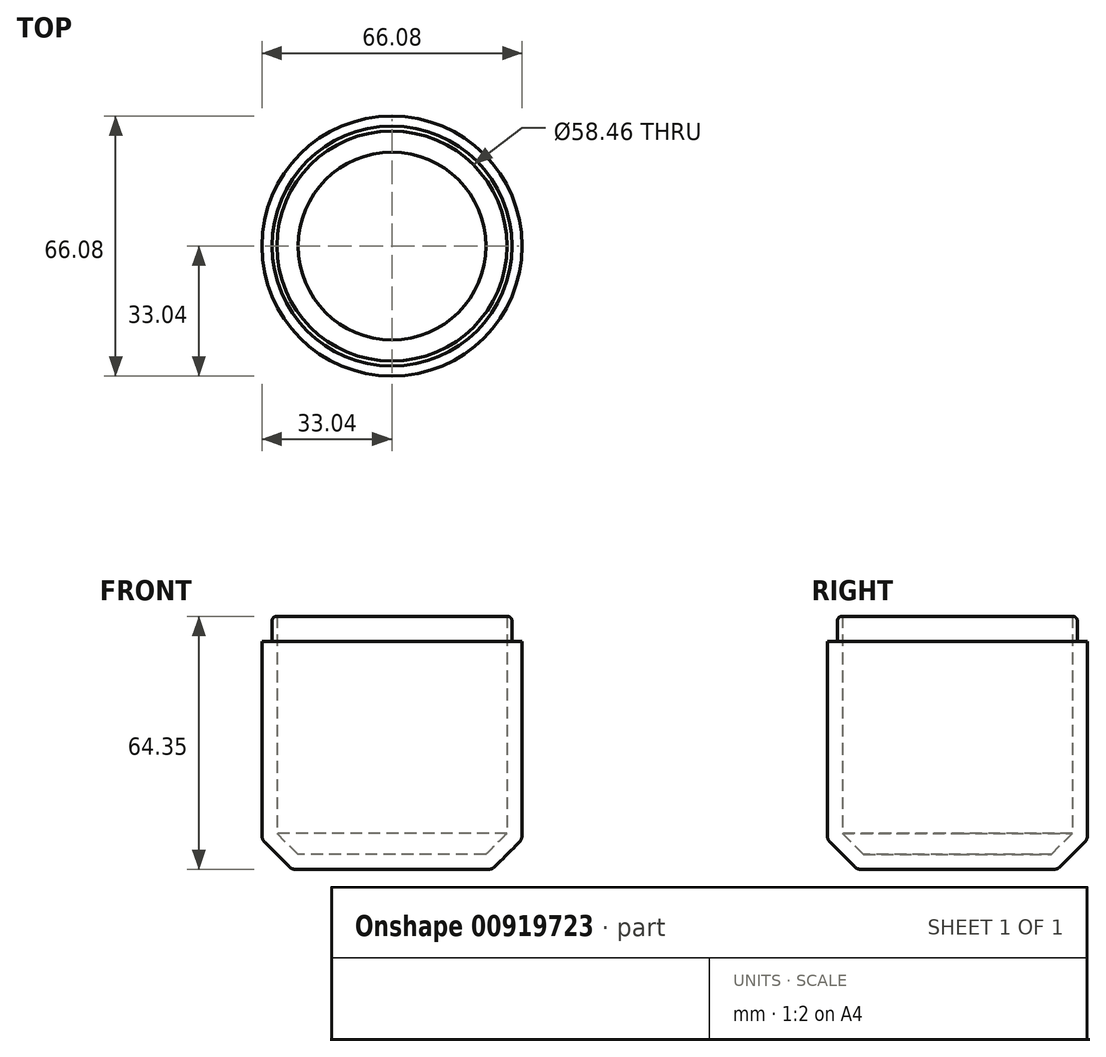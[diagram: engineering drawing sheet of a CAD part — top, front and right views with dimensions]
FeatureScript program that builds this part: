
annotation { "Feature Type Name" : "Feature", "Feature Type Description" : "" }
export const myFeature = defineFeature(function(context is Context, id is Id, definition is map)
    precondition{}
    {
        {
            var Q0;
            Q0=qCreatedBy(makeId("Top.planeOp"),FACE);
            var sketch = newSketch(context, id + "F0", { "sketchPlane" : qUnion([Q0])});
            skCircle(sketch, "E0", {"center": v(0, 0) * mm, "radius": 33.04 * mm});
            skSolve(sketch);
        }
        {
            var Q0;
            Q0 = qSketchRegion(id + "F0", true);
            extrude(context, id + "F1", {"entities" : qUnion([Q0]), "depth" : 58 * mm, "offsetDistance" : 25.4 * mm});
        }
        {
            var Q0;
            Q0=makeQuery(id+"F1.opExtrude","CAP_EDGE",EDGE,{"disambiguationData":[OSD([sQuery(id+"F0.wireOp",EDGE,"E0")])],"isStart":true});
            chamfer(context, id + "F2", {"entities" : qUnion([Q0]), "width" : 7.62 * mm, "tangentPropagation" : true});
        }
        {
            var Q0;
            Q0=makeQuery(id+"F1.opExtrude","CAP_FACE",FACE,{"disambiguationData":[OSD([sQuery(id+"F0.wireOp",EDGE,"E0")])],"isStart":false});
            shell(context, id + "F3", {"entities" : qUnion([Q0]), "thickness" : 3.8 * mm});
        }
        {
            var Q0;
            {var subQ0=sQuery(id+"F0.wireOp",EDGE,"E0");Q0=makeQuery(id+"F2.opChamfer","BLEND_EDGE",EDGE,{"blendedFrom":[makeQuery(id+"F1.opExtrude","CAP_EDGE",EDGE,{"disambiguationData":[OSD([subQ0])],"isStart":true}),makeQuery(id+"F1.opExtrude","SWEPT_FACE",FACE,{"disambiguationData":[OSD([subQ0])]})],"blendedInto":[makeQuery(id+"F1.opExtrude","SWEPT_FACE",FACE,{"disambiguationData":[OSD([subQ0])]})]});}
            var Q1;
            {var subQ0=sQuery(id+"F0.wireOp",EDGE,"E0");Q1=makeQuery(id+"F2.opChamfer","BLEND_EDGE",EDGE,{"blendedFrom":[makeQuery(id+"F1.opExtrude","CAP_EDGE",EDGE,{"disambiguationData":[OSD([subQ0])],"isStart":true}),makeQuery(id+"F1.opExtrude","CAP_FACE",FACE,{"disambiguationData":[OSD([subQ0])],"isStart":true})],"blendedInto":[makeQuery(id+"F1.opExtrude","CAP_FACE",FACE,{"disambiguationData":[OSD([subQ0])],"isStart":true})]});}
            fillet(context, id + "F4", {"entities" : qUnion([Q0, Q1]), "radius" : 2.54 * mm, "tangentPropagation" : true, "allowEdgeOverflow" : false});
        }
        {
            var Q0;
            Q0=makeQuery(id+"F1.opExtrude","CAP_FACE",FACE,{"disambiguationData":[OSD([sQuery(id+"F0.wireOp",EDGE,"E0")])],"isStart":false});
            var sketch = newSketch(context, id + "F5", { "sketchPlane" : qUnion([Q0])});
            skCircle(sketch, "E1", {"center": v(0, 0) * mm, "radius": 30.5 * mm});
            skCircle(sketch, "E2.0", {"center": v(0, 0) * mm, "radius": 29.23 * mm});
            skSolve(sketch);
        }
        {
            var Q0;
            Q0 = qSketchRegion(id + "F5", true);
            extrude(context, id + "F6", {"entities" : qUnion([Q0]), "operationType" : NewBodyOperationType.ADD, "depth" : 6.35 * mm, "offsetDistance" : 25.4 * mm});
        }
        {
            var Q0;
            Q0=makeQuery(id+"F6.opExtrude","CAP_EDGE",EDGE,{"disambiguationData":[OSD([sQuery(id+"F5.wireOp",EDGE,"E1")])],"isStart":false});
            fillet(context, id + "F7", {"entities" : qUnion([Q0]), "radius" : 1.27 * mm, "tangentPropagation" : true, "allowEdgeOverflow" : false});
        }
    });
